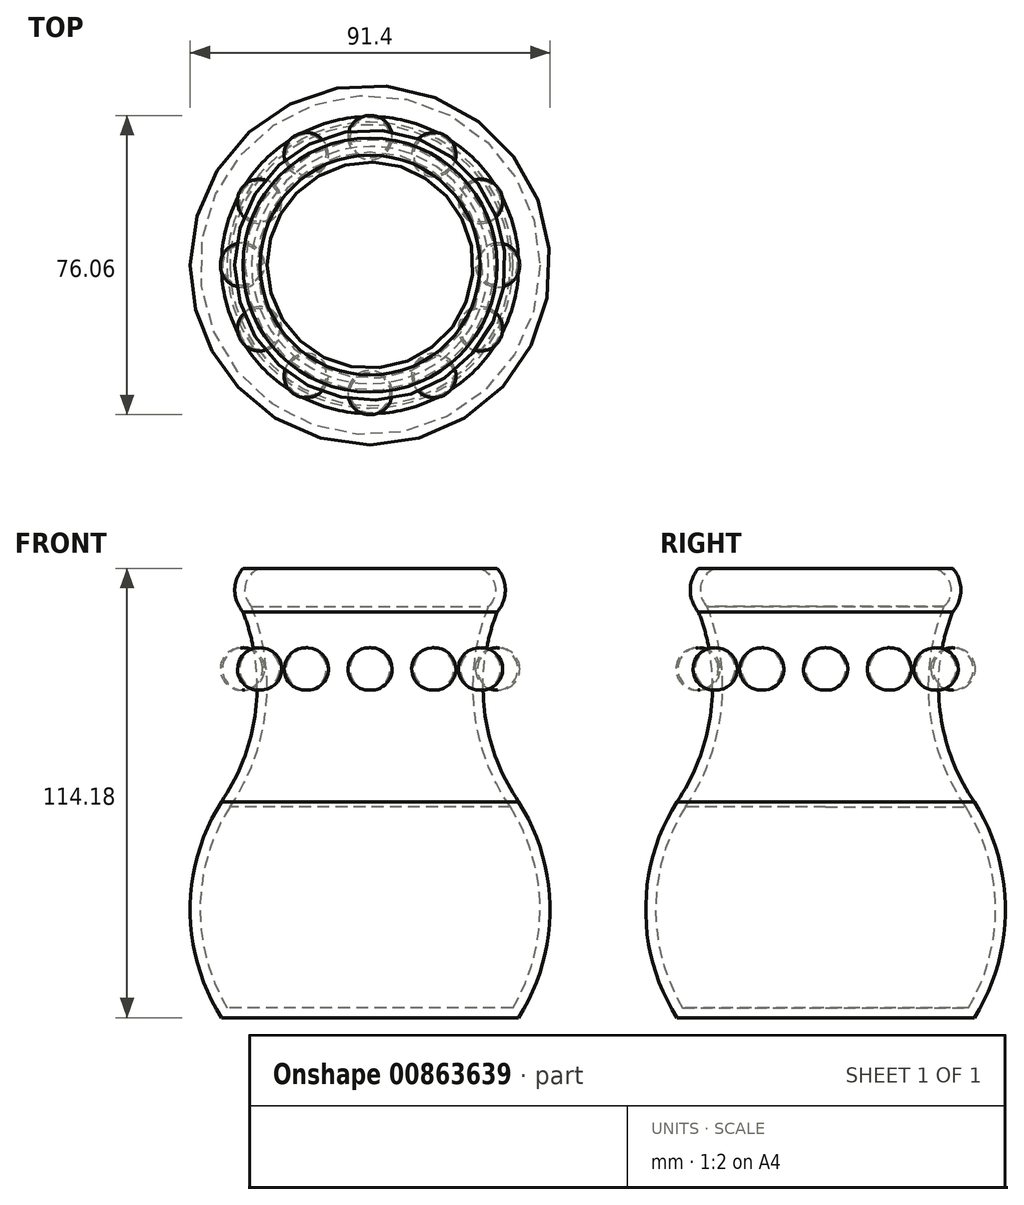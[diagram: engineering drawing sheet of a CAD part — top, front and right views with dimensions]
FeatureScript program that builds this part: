
annotation { "Feature Type Name" : "Feature", "Feature Type Description" : "" }
export const myFeature = defineFeature(function(context is Context, id is Id, definition is map)
    precondition{}
    {
        {
            var Q0;
            Q0=qCreatedBy(makeId("Front.planeOp"),FACE);
            var sketch = newSketch(context, id + "F0", { "sketchPlane" : qUnion([Q0])});
            skLineSegment(sketch, "E0", {"start": v(0, 57.77) * mm, "end": v(32.3, 57.77) * mm});
            skArc(sketch, "E1", {"start": v(32.3, 46.7) * mm, "mid": v(34.37, 52.23) * mm, "end": v(32.3, 57.77) * mm});
            skArc(sketch, "E2", {"start": v(32.3, 46.7) * mm, "mid": v(29.04, 21.9) * mm, "end": v(37.75, -1.53) * mm});
            skArc(sketch, "E3", {"start": v(37.75, -56.4) * mm, "mid": v(45.7, -28.97) * mm, "end": v(37.75, -1.53) * mm});
            skLineSegment(sketch, "E4", {"start": v(37.75, -56.4) * mm, "end": v(0, -56.4) * mm});
            skLineSegment(sketch, "E5", {"start": v(0, -56.4) * mm, "end": v(0, 57.77) * mm});
            skSolve(sketch);
        }
        {
            var Q0;
            Q0=makeQuery(id+"F0.imprint","IMPRINT",FACE,{"disambiguationData":[TD([[makeQuery(id+"F0.imprint","IMPRINT",EDGE,{"derivedFrom":sQuery(id+"F0.wireOp",EDGE,"E0")}),-1.0]])]});
            var Q1;
            Q1=sQuery(id+"F0.wireOp",EDGE,"E5");
            revolve(context, id + "F1", {"surfaceOperationType" : NewSurfaceOperationType.NEW, "entities" : qUnion([Q0]), "axis" : qUnion([Q1]), "revolveType" : RevolveType.FULL});
        }
        {
            var Q0;
            Q0=makeQuery(id+"F1.opRevolve","SWEPT_FACE",FACE,{"disambiguationData":[OSD([sQuery(id+"F0.wireOp",EDGE,"E0")])]});
            shell(context, id + "F2", {"entities" : qUnion([Q0]), "thickness" : 2.54 * mm});
        }
        {
            var Q0;
            Q0=qCreatedBy(makeId("Front.planeOp"),FACE);
            var sketch = newSketch(context, id + "F3", { "sketchPlane" : qUnion([Q0])});
            skArc(sketch, "E6", {"start": v(82.2, 7) * mm, "mid": v(87.57, 12.15) * mm, "end": v(82.68, 17.75) * mm});
            skLineSegment(sketch, "E7", {"start": v(82.68, 17.75) * mm, "end": v(82.2, 7) * mm});
            skSolve(sketch);
        }
        {
            var Q0;
            Q0=makeQuery(id+"F3.imprint","IMPRINT",FACE,{"disambiguationData":[TD([[makeQuery(id+"F3.imprint","IMPRINT",EDGE,{"derivedFrom":sQuery(id+"F3.wireOp",EDGE,"E6")}),1.0]])]});
            var Q1;
            Q1=sQuery(id+"F3.wireOp",EDGE,"E7");
            revolve(context, id + "F4", {"surfaceOperationType" : NewSurfaceOperationType.NEW, "entities" : qUnion([Q0]), "axis" : qUnion([Q1]), "revolveType" : RevolveType.FULL});
        }
        {
            var Q0;
            Q0=makeQuery(id+"F4.opRevolve","SWEPT_BODY",BODY,{"disambiguationData":[OSD([sQuery(id+"F3.wireOp",EDGE,"E6"),sQuery(id+"F3.wireOp",EDGE,"E7")])]});
            transform(context, id + "F5", {"entities" : qUnion([Q0]), "transformType" : TransformType.TRANSLATION_3D, "dx" : -50.04 * mm, "dy" : 0 * mm, "dz" : 19.8 * mm, "makeCopy" : false});
        }
        {
            var Q0;
            Q0=makeQuery(id+"F4.opRevolve","SWEPT_BODY",BODY,{"disambiguationData":[OSD([sQuery(id+"F3.wireOp",EDGE,"E6"),sQuery(id+"F3.wireOp",EDGE,"E7")])]});
            var Q1;
            Q1=makeQuery(id+"F1.opRevolve","SWEPT_FACE",FACE,{"disambiguationData":[OSD([sQuery(id+"F0.wireOp",EDGE,"E1")])]});
            circularPattern(context, id + "F6", {"entities" : qUnion([Q0]), "axis" : qUnion([Q1]), "angle" : 360 * degree, "instanceCount" : 12, "equalSpace" : true});
        }
    });
